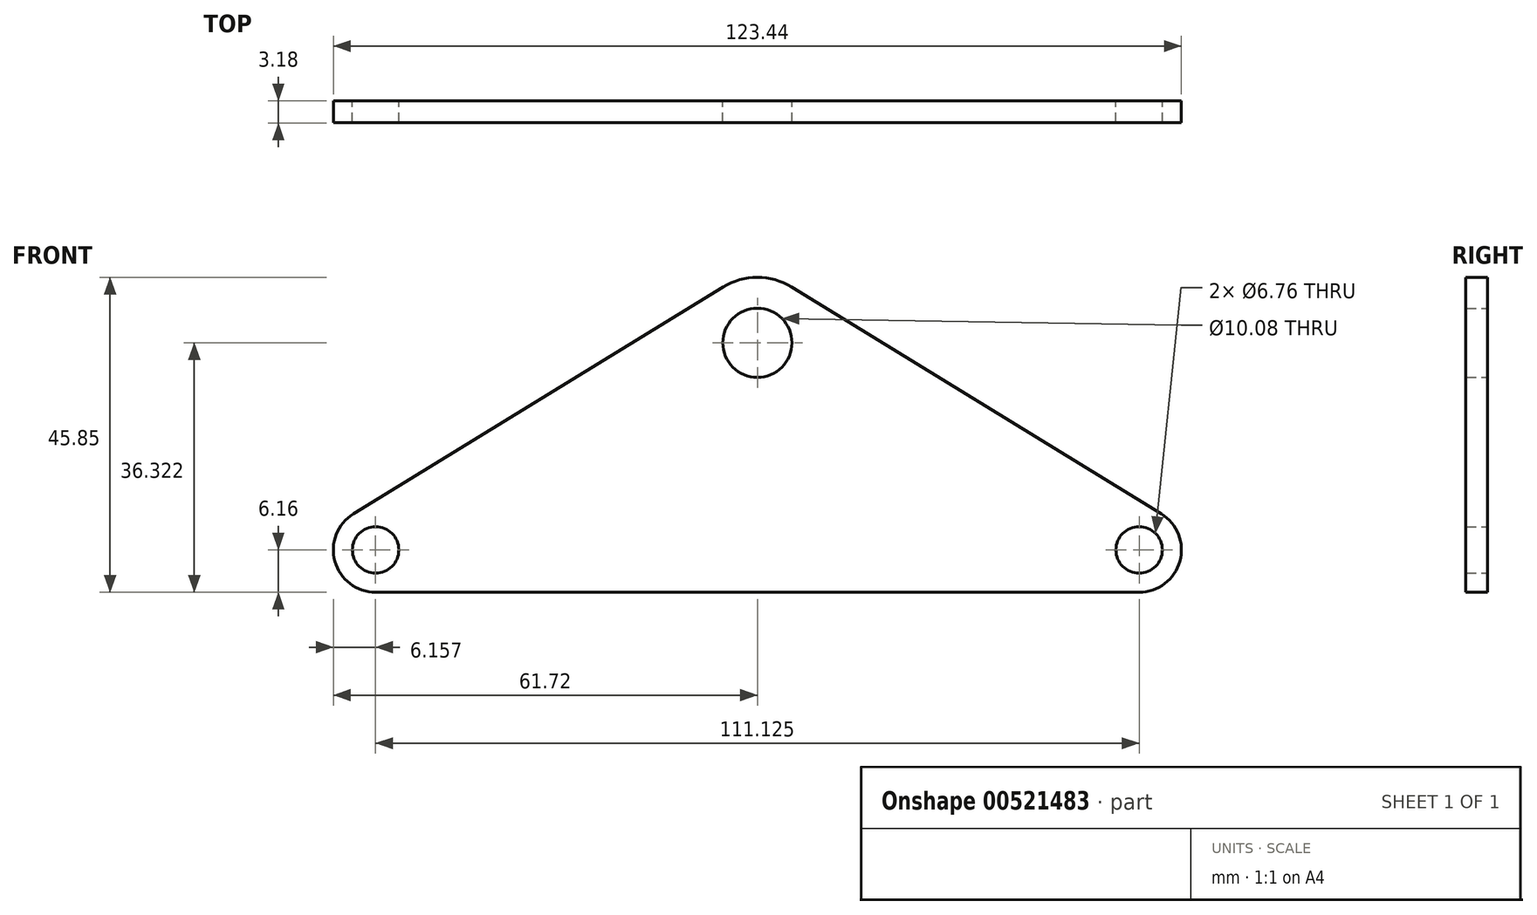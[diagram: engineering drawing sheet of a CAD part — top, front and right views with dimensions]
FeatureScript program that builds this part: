
annotation { "Feature Type Name" : "Feature", "Feature Type Description" : "" }
export const myFeature = defineFeature(function(context is Context, id is Id, definition is map)
    precondition{}
    {
        {
            var Q0;
            Q0=qCreatedBy(makeId("Front.planeOp"),FACE);
            var sketch = newSketch(context, id + "F0", { "sketchPlane" : qUnion([Q0])});
            skLineSegment(sketch, "E0", {"start": v(-58.79, 11.4) * mm, "end": v(-4.98, 44.44) * mm});
            skArc(sketch, "E1", {"start": v(0, 45.85) * mm, "mid": v(-2.59, 45.49) * mm, "end": v(-4.98, 44.44) * mm});
            skLineSegment(sketch, "E2", {"start": v(0, 0) * mm, "end": v(-55.56, 0) * mm});
            skArc(sketch, "E3", {"start": v(-58.79, 11.4) * mm, "mid": v(-61.5, 4.49) * mm, "end": v(-55.56, 0) * mm});
            skLineSegment(sketch, "E4.MirrorCS", {"start": v(0, 0) * mm, "end": v(55.56, 0) * mm});
            skArc(sketch, "E5.MirrorCS", {"start": v(58.79, 11.4) * mm, "mid": v(61.5, 4.49) * mm, "end": v(55.56, 0) * mm});
            skArc(sketch, "E6.MirrorCS", {"start": v(0, 45.85) * mm, "mid": v(2.59, 45.49) * mm, "end": v(4.98, 44.44) * mm});
            skLineSegment(sketch, "E7.MirrorCS", {"start": v(58.79, 11.4) * mm, "end": v(4.98, 44.44) * mm});
            skSolve(sketch);
        }
        {
            var Q0;
            Q0=makeQuery(id+"F0.imprint","IMPRINT",FACE,{"disambiguationData":[TD([[makeQuery(id+"F0.imprint","IMPRINT",EDGE,{"derivedFrom":sQuery(id+"F0.wireOp",EDGE,"E0")}),-1.0]])]});
            extrude(context, id + "F1", {"entities" : qUnion([Q0]), "depth" : 3.17 * mm, "offsetDistance" : 25.4 * mm});
        }
        {
            var Q0;
            Q0=sQuery(id+"F0.wireOp",VERTEX,"E1.center");
            var Q1;
            Q1=makeQuery(id+"F1.opExtrude","SWEPT_BODY",BODY,{"disambiguationData":[OSD([sQuery(id+"F0.wireOp",EDGE,"E0"),sQuery(id+"F0.wireOp",EDGE,"E1"),sQuery(id+"F0.wireOp",EDGE,"E2"),sQuery(id+"F0.wireOp",EDGE,"E3"),sQuery(id+"F0.wireOp",EDGE,"E4.MirrorCS"),sQuery(id+"F0.wireOp",EDGE,"E5.MirrorCS"),sQuery(id+"F0.wireOp",EDGE,"E6.MirrorCS"),sQuery(id+"F0.wireOp",EDGE,"E7.MirrorCS")])]});
            hole(context, id + "F2", {"style" : HoleStyle.SIMPLE, "endStyle" : HoleEndStyle.THROUGH, "oppositeDirection" : true, "standardTappedOrClearance" : lookupTablePath({ "standard" : "ANSI", "fit" : "Normal (ASME)", "size" : "3/8", "type" : "Clearance" }), "standardBlindInLast" : lookupTablePath({ "fit" : "Free", "standard" : "ANSI", "size" : "3/8", "type" : "Clearance" }), "holeDiameter" : 10.08 * mm, "isTappedThrough" : true, "tappedDepth" : 12.7 * mm, "tapClearance" : 3, "startFromSketch" : true, "locations" : qUnion([Q0]), "scope" : qUnion([Q1])});
        }
        {
            var Q0;
            Q0=sQuery(id+"F0.wireOp",VERTEX,"E5.MirrorCS.center");
            var Q1;
            Q1=sQuery(id+"F0.wireOp",VERTEX,"E3.center");
            var Q2;
            Q2=makeQuery(id+"F1.opExtrude","SWEPT_BODY",BODY,{"disambiguationData":[OSD([sQuery(id+"F0.wireOp",EDGE,"E0"),sQuery(id+"F0.wireOp",EDGE,"E1"),sQuery(id+"F0.wireOp",EDGE,"E2"),sQuery(id+"F0.wireOp",EDGE,"E3"),sQuery(id+"F0.wireOp",EDGE,"E4.MirrorCS"),sQuery(id+"F0.wireOp",EDGE,"E5.MirrorCS"),sQuery(id+"F0.wireOp",EDGE,"E6.MirrorCS"),sQuery(id+"F0.wireOp",EDGE,"E7.MirrorCS")])]});
            hole(context, id + "F3", {"style" : HoleStyle.SIMPLE, "endStyle" : HoleEndStyle.THROUGH, "oppositeDirection" : true, "standardTappedOrClearance" : lookupTablePath({ "standard" : "ANSI", "fit" : "Normal (ASME)", "size" : "1/4", "type" : "Clearance" }), "standardBlindInLast" : lookupTablePath({ "fit" : "Free", "standard" : "ANSI", "size" : "1/4", "type" : "Clearance" }), "holeDiameter" : 6.76 * mm, "isTappedThrough" : true, "tappedDepth" : 12.7 * mm, "tapClearance" : 3, "startFromSketch" : true, "locations" : qUnion([Q0, Q1]), "scope" : qUnion([Q2])});
        }
    });
